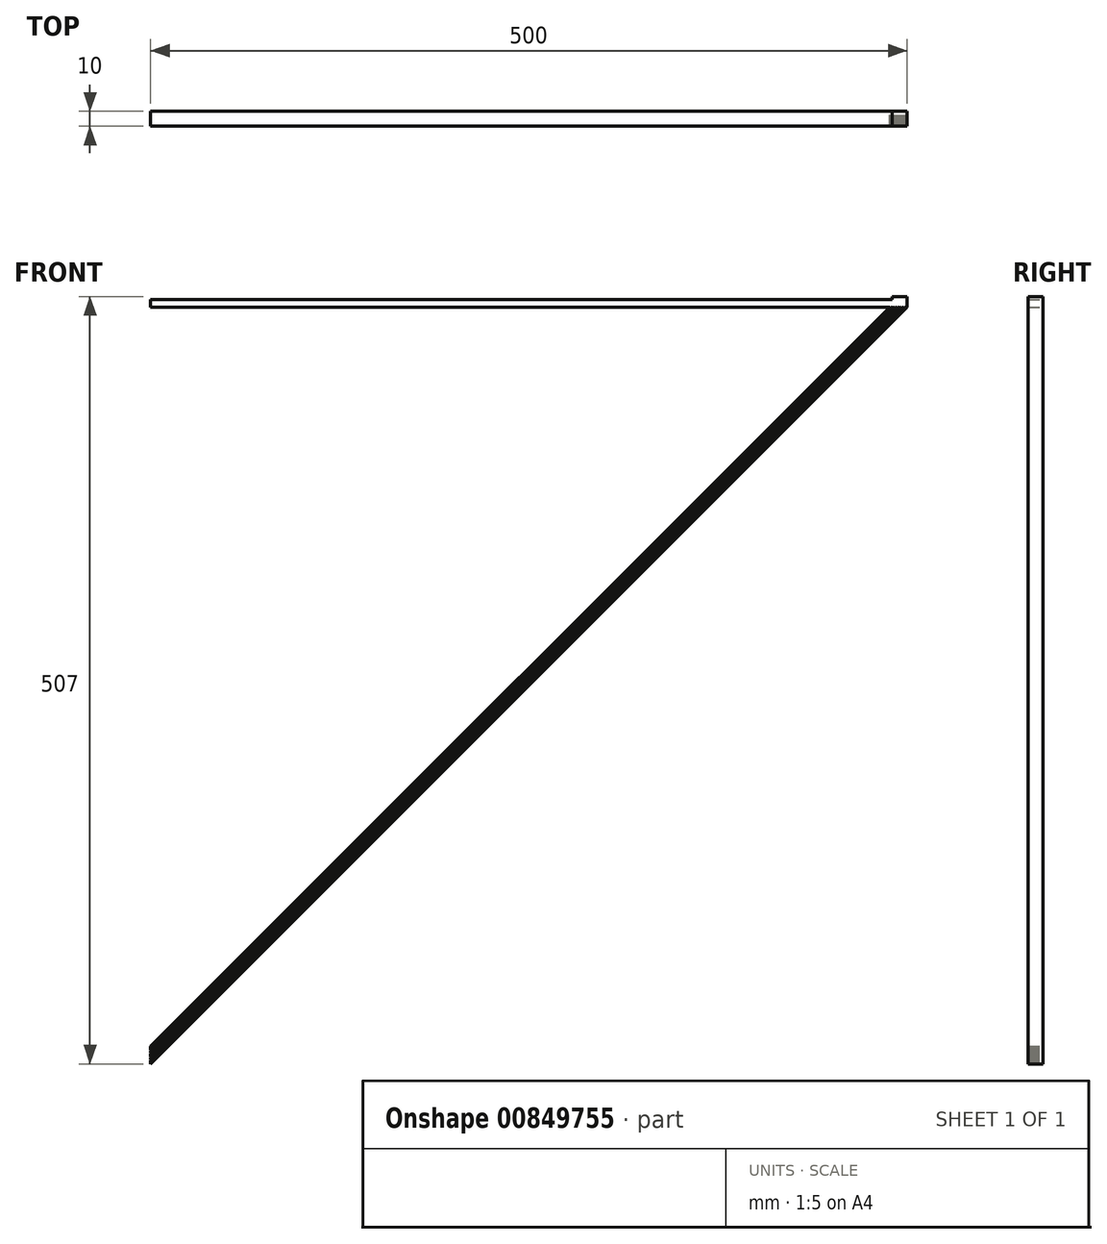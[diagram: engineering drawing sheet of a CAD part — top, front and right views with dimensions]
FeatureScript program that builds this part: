
annotation { "Feature Type Name" : "Feature", "Feature Type Description" : "" }
export const myFeature = defineFeature(function(context is Context, id is Id, definition is map)
    precondition{}
    {
        {
            var Q0;
            Q0=qCreatedBy(makeId("Front.planeOp"),FACE);
            var sketch = newSketch(context, id + "F0", { "sketchPlane" : qUnion([Q0])});
            skLineSegment(sketch, "E0.right", {"start": v(249.85, 318.38) * mm, "end": v(249.85, 313.38) * mm});
            skLineSegment(sketch, "E1", {"start": v(249.85, 318.38) * mm, "end": v(-250.15, 318.38) * mm});
            skLineSegment(sketch, "E2", {"start": v(-250.15, 318.38) * mm, "end": v(-250.15, 313.38) * mm});
            skLineSegment(sketch, "E3", {"start": v(249.85, 313.38) * mm, "end": v(-250.15, 313.38) * mm});
            skLineSegment(sketch, "E4", {"start": v(249.85, 313.38) * mm, "end": v(-250.15, -186.62) * mm});
            skLineSegment(sketch, "E5", {"start": v(249.85, 313.38) * mm, "end": v(248.85, 313.38) * mm});
            skLineSegment(sketch, "E6", {"start": v(248.85, 313.38) * mm, "end": v(248.35, 313.38) * mm});
            skLineSegment(sketch, "E7", {"start": v(248.35, 313.38) * mm, "end": v(247.35, 313.38) * mm});
            skLineSegment(sketch, "E8", {"start": v(-250.15, -186.62) * mm, "end": v(-250.15, -185.62) * mm});
            skLineSegment(sketch, "E9", {"start": v(-250.15, -185.62) * mm, "end": v(-250.15, -185.12) * mm});
            skLineSegment(sketch, "E10", {"start": v(-250.15, -185.12) * mm, "end": v(-250.15, -184.12) * mm});
            skLineSegment(sketch, "E11", {"start": v(248.85, 313.38) * mm, "end": v(-250.15, -185.62) * mm});
            skLineSegment(sketch, "E12", {"start": v(-250.15, -185.12) * mm, "end": v(248.35, 313.38) * mm});
            skLineSegment(sketch, "E13", {"start": v(247.35, 313.38) * mm, "end": v(-250.15, -184.12) * mm});
            skLineSegment(sketch, "E14", {"start": v(-250.15, -184.12) * mm, "end": v(-250.15, -183.62) * mm});
            skLineSegment(sketch, "E15", {"start": v(-250.15, -183.62) * mm, "end": v(-250.15, -182.62) * mm});
            skLineSegment(sketch, "E16", {"start": v(-250.15, -182.62) * mm, "end": v(-250.15, -182.12) * mm});
            skLineSegment(sketch, "E17", {"start": v(-250.15, -182.12) * mm, "end": v(-250.15, -181.12) * mm});
            skLineSegment(sketch, "E18", {"start": v(247.35, 313.38) * mm, "end": v(246.85, 313.38) * mm});
            skLineSegment(sketch, "E19", {"start": v(246.85, 313.38) * mm, "end": v(245.85, 313.38) * mm});
            skLineSegment(sketch, "E20", {"start": v(245.85, 313.38) * mm, "end": v(245.35, 313.38) * mm});
            skLineSegment(sketch, "E21", {"start": v(245.35, 313.38) * mm, "end": v(244.35, 313.38) * mm});
            skLineSegment(sketch, "E22", {"start": v(246.85, 313.38) * mm, "end": v(-250.15, -183.62) * mm});
            skLineSegment(sketch, "E23", {"start": v(-250.15, -182.62) * mm, "end": v(245.85, 313.38) * mm});
            skLineSegment(sketch, "E24", {"start": v(245.35, 313.38) * mm, "end": v(-250.15, -182.12) * mm});
            skLineSegment(sketch, "E25", {"start": v(-250.15, -181.12) * mm, "end": v(244.35, 313.38) * mm});
            skLineSegment(sketch, "E26", {"start": v(244.35, 313.38) * mm, "end": v(243.85, 313.38) * mm});
            skLineSegment(sketch, "E27", {"start": v(243.85, 313.38) * mm, "end": v(242.85, 313.38) * mm});
            skLineSegment(sketch, "E28", {"start": v(242.85, 313.38) * mm, "end": v(242.35, 313.38) * mm});
            skLineSegment(sketch, "E29", {"start": v(242.35, 313.38) * mm, "end": v(241.35, 313.38) * mm});
            skLineSegment(sketch, "E30", {"start": v(241.35, 313.38) * mm, "end": v(240.85, 313.38) * mm});
            skLineSegment(sketch, "E31", {"start": v(240.85, 313.38) * mm, "end": v(239.85, 313.38) * mm});
            skLineSegment(sketch, "E32", {"start": v(-250.15, -181.12) * mm, "end": v(-250.15, -180.62) * mm});
            skLineSegment(sketch, "E33", {"start": v(-250.15, -180.62) * mm, "end": v(-250.15, -179.62) * mm});
            skLineSegment(sketch, "E34", {"start": v(-250.15, -179.62) * mm, "end": v(-250.15, -179.12) * mm});
            skLineSegment(sketch, "E35", {"start": v(-250.15, -179.12) * mm, "end": v(-250.15, -178.12) * mm});
            skLineSegment(sketch, "E36", {"start": v(-250.15, -178.12) * mm, "end": v(-250.15, -177.62) * mm});
            skLineSegment(sketch, "E37", {"start": v(-250.15, -177.62) * mm, "end": v(-250.15, -176.62) * mm});
            skLineSegment(sketch, "E38", {"start": v(-250.15, -180.62) * mm, "end": v(243.85, 313.38) * mm});
            skLineSegment(sketch, "E39", {"start": v(242.85, 313.38) * mm, "end": v(-250.15, -179.62) * mm});
            skLineSegment(sketch, "E40", {"start": v(-250.15, -179.12) * mm, "end": v(242.35, 313.38) * mm});
            skLineSegment(sketch, "E41", {"start": v(241.35, 313.38) * mm, "end": v(-250.15, -178.12) * mm});
            skLineSegment(sketch, "E42", {"start": v(-250.15, -177.62) * mm, "end": v(240.85, 313.38) * mm});
            skLineSegment(sketch, "E43", {"start": v(239.85, 313.38) * mm, "end": v(-250.15, -176.62) * mm});
            skLineSegment(sketch, "E44", {"start": v(-250.15, -176.62) * mm, "end": v(-250.15, -176.12) * mm});
            skLineSegment(sketch, "E45", {"start": v(-250.15, -176.12) * mm, "end": v(-250.15, -175.12) * mm});
            skLineSegment(sketch, "E46", {"start": v(239.85, 313.38) * mm, "end": v(239.35, 313.38) * mm});
            skLineSegment(sketch, "E47", {"start": v(239.35, 313.38) * mm, "end": v(238.35, 313.38) * mm});
            skLineSegment(sketch, "E48", {"start": v(239.35, 313.38) * mm, "end": v(-250.15, -176.12) * mm});
            skLineSegment(sketch, "E49", {"start": v(-250.15, -175.12) * mm, "end": v(238.35, 313.38) * mm});
            skSolve(sketch);
        }
        {
            var Q0;
            {var subQ5=sQuery(id+"F0.wireOp",EDGE,"E0.right");Q0=makeQuery(id+"F0.imprint","IMPRINT",FACE,{"disambiguationData":[TD([[makeQuery(id+"F0.imprint","IMPRINT",EDGE,{"derivedFrom":subQ5}),-1.0]])]});}
            var Q1;
            Q1=makeQuery(id+"F0.imprint","IMPRINT",FACE,{"disambiguationData":[TD([[makeQuery(id+"F0.imprint","IMPRINT",EDGE,{"derivedFrom":sQuery(id+"F0.wireOp",EDGE,"E10")}),-1.0]])]});
            var Q2;
            {var subQ0=sQuery(id+"F0.wireOp",EDGE,"E4");Q2=makeQuery(id+"F0.imprint","IMPRINT",FACE,{"disambiguationData":[TD([[makeQuery(id+"F0.imprint","IMPRINT",EDGE,{"derivedFrom":subQ0}),-1.0]])]});}
            var Q3;
            Q3=makeQuery(id+"F0.imprint","IMPRINT",FACE,{"disambiguationData":[TD([[makeQuery(id+"F0.imprint","IMPRINT",EDGE,{"derivedFrom":sQuery(id+"F0.wireOp",EDGE,"E17")}),-1.0]])]});
            var Q4;
            Q4=makeQuery(id+"F0.imprint","IMPRINT",FACE,{"disambiguationData":[TD([[makeQuery(id+"F0.imprint","IMPRINT",EDGE,{"derivedFrom":sQuery(id+"F0.wireOp",EDGE,"E15")}),-1.0]])]});
            var Q5;
            Q5=makeQuery(id+"F0.imprint","IMPRINT",FACE,{"disambiguationData":[TD([[makeQuery(id+"F0.imprint","IMPRINT",EDGE,{"derivedFrom":sQuery(id+"F0.wireOp",EDGE,"E37")}),-1.0]])]});
            var Q6;
            Q6=makeQuery(id+"F0.imprint","IMPRINT",FACE,{"disambiguationData":[TD([[makeQuery(id+"F0.imprint","IMPRINT",EDGE,{"derivedFrom":sQuery(id+"F0.wireOp",EDGE,"E35")}),-1.0]])]});
            var Q7;
            Q7=makeQuery(id+"F0.imprint","IMPRINT",FACE,{"disambiguationData":[TD([[makeQuery(id+"F0.imprint","IMPRINT",EDGE,{"derivedFrom":sQuery(id+"F0.wireOp",EDGE,"E33")}),-1.0]])]});
            var Q8;
            Q8=makeQuery(id+"F0.imprint","IMPRINT",FACE,{"disambiguationData":[TD([[makeQuery(id+"F0.imprint","IMPRINT",EDGE,{"derivedFrom":sQuery(id+"F0.wireOp",EDGE,"E45")}),-1.0]])]});
            extrude(context, id + "F1", {"entities" : qUnion([Q0, Q1, Q2, Q3, Q4, Q5, Q6, Q7, Q8]), "endBound" : BoundingType.SYMMETRIC, "depth" : 10 * mm, "offsetDistance" : 25 * mm});
        }
        {
            var Q0;
            Q0=makeQuery(id+"F1.opExtrude","SWEPT_FACE",FACE,{"disambiguationData":[OSD([sQuery(id+"F0.wireOp",EDGE,"E1")])]});
            var sketch = newSketch(context, id + "F2", { "sketchPlane" : qUnion([Q0])});
            skLineSegment(sketch, "E50.left", {"start": v(249.85, -5) * mm, "end": v(249.85, 5) * mm});
            skSolve(sketch);
        }
        {
            var Q0;
            Q0=makeQuery(id+"F1.opExtrude","SWEPT_FACE",FACE,{"disambiguationData":[OSD([sQuery(id+"F0.wireOp",EDGE,"E1")])]});
            var sketch = newSketch(context, id + "F3", { "sketchPlane" : qUnion([Q0])});
            skLineSegment(sketch, "E51.bottom", {"start": v(249.85, -5) * mm, "end": v(239.85, -5) * mm});
            skLineSegment(sketch, "E51.top", {"start": v(249.85, 5) * mm, "end": v(239.85, 5) * mm});
            skLineSegment(sketch, "E51.left", {"start": v(249.85, -5) * mm, "end": v(249.85, 5) * mm});
            skLineSegment(sketch, "E51.right", {"start": v(239.85, -5) * mm, "end": v(239.85, 5) * mm});
            skSolve(sketch);
        }
        {
            var Q0;
            Q0 = qSketchRegion(id + "F3", true);
            var Q1;
            Q1 = qSketchRegion(id + "F2", true);
            extrude(context, id + "F4", {"entities" : qUnion([Q0, Q1]), "operationType" : NewBodyOperationType.ADD, "depth" : 2 * mm, "offsetDistance" : 25 * mm});
        }
        {
            var Q0;
            Q0=makeQuery(id+"F4.opExtrude","CAP_EDGE",EDGE,{"disambiguationData":[OSD([sQuery(id+"F3.wireOp",EDGE,"E51.right")])],"isStart":true});
            var Q1;
            Q1=makeQuery(id+"F1.opExtrude","SWEPT_EDGE",EDGE,{"disambiguationData":[OSD([sQuery(id+"F0.wireOp",EDGE,"E0.right"),sQuery(id+"F0.wireOp",EDGE,"E3"),sQuery(id+"F0.wireOp",EDGE,"E4")])]});
            fillet(context, id + "F5", {"entities" : qUnion([Q0, Q1]), "radius" : 0.5 * mm, "tangentPropagation" : true, "allowEdgeOverflow" : false});
        }
    });
